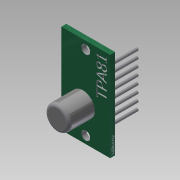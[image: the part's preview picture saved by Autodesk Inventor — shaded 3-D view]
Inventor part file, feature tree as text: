
AUTODESK INVENTOR PART (.ipt)
format: ipt  version: 2015 SP1 (Build 190203100, 203)  size: 445,440 bytes
history: native  units: mm
features: sketch x9, extrude x6, plane x3, fillet x1
ambient origin geometry x8: Origin, YZ Plane, XZ Plane, XY Plane, X Axis, Y Axis, Z Axis, Center Point
bodies: Solid1 (feature_tree)
feature tree (19):
  sketch  "Sketch1"  dims[d0=16.6mm d1=30.4mm]
  extrude  "Extrusion1"  Depth=30.4mm
  extrude  "Extrusion2"  Depth=3.0mm
  fillet  "Fillet1"  Radius=2.54mm
  sketch  "Sketch2"  dims[d2=3.0mm d3=3.0mm d4=2.54mm]
  sketch  "Sketch3"  dims[d5=2.54mm d6=8.18mm]
  extrude  "Extrusion3"  Depth=8.18mm
  extrude  "Extrusion4"  Depth=11.3mm
  sketch  "Sketch4"  dims[d7=7.3mm d8=11.3mm]
  extrude  "Extrusion5"  Depth=10.5mm TaperAngle=0.0deg
  extrude  "Extrusion6"  Depth=1.0mm
  plane  "Work Plane1"
  sketch  "Sketch8"  dims[d29=1.0mm d30=1.0mm]
  plane  "Work Plane2"
  sketch  "Sketch9"  dims[d31=1.0mm]
  plane  "Work Plane3"
  sketch  "Sketch10"  dims[d32=1.0mm]
  sketch  "Sketch11"  dims[d33=1.0mm d34=1.0mm d35=1.0mm d36=1.0mm d37=2.54mm d38=2.54mm d39=2.54mm d40=2.54mm d41=2.54mm d43=2.54mm d44=5.4mm d45=10.0mm d46=0.0mm d47=1.0mm d48=2.54mm d49=2.54mm d50=10.0mm d51=0.0mm d52=1.0mm d53=0.0mm d54=1.0mm d55=0.0mm d56=-1.0mm d57=3.9mm d58=10.5mm d59=200.0mm d60=90.0deg d61=200.0mm d62=16.231562mm d63=200.0mm d64=15.184364mm d65=200.0mm d66=0.893609mm d67=200.0mm d68=1.787217mm d69=200.0mm d70=2.680826mm d71=200.0mm d72=3.574434mm]
  sketch  "Sketch5"  dims[d9=1.7mm d10=0.0mm d11=10.5mm d12=0.0mm]
